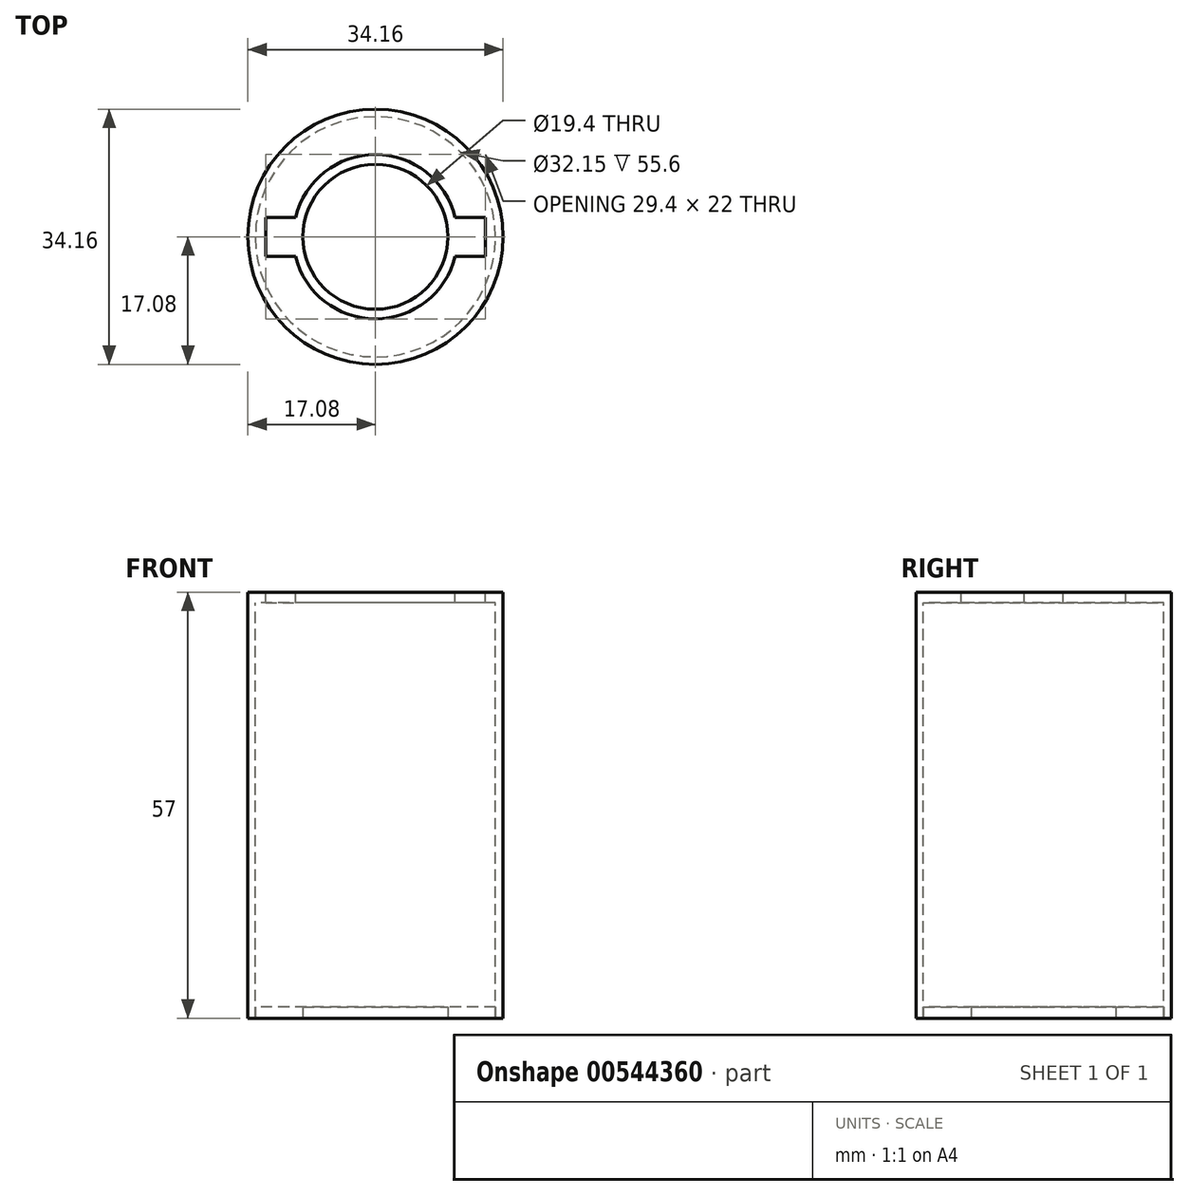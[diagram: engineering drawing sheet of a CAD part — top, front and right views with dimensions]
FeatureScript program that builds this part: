
annotation { "Feature Type Name" : "Feature", "Feature Type Description" : "" }
export const myFeature = defineFeature(function(context is Context, id is Id, definition is map)
    precondition{}
    {
        {
            var Q0;
            Q0=qCreatedBy(makeId("Top.planeOp"),FACE);
            var sketch = newSketch(context, id + "F0", { "sketchPlane" : qUnion([Q0])});
            skCircle(sketch, "E0", {"center": v(0, 0) * mm, "radius": 17.07 * mm});
            skCircle(sketch, "E1", {"center": v(0, 0) * mm, "radius": 16.07 * mm});
            skSolve(sketch);
        }
        {
            var Q0;
            Q0=makeQuery(id+"F0.imprint","IMPRINT",FACE,{"disambiguationData":[TD([[makeQuery(id+"F0.imprint","IMPRINT",EDGE,{"derivedFrom":sQuery(id+"F0.wireOp",EDGE,"E0")}),1.0]])]});
            extrude(context, id + "F1", {"entities" : qUnion([Q0]), "oppositeDirection" : true, "depth" : 57 * mm, "offsetDistance" : 25 * mm});
        }
        {
            var Q0;
            Q0=makeQuery(id+"F1.opExtrude","CAP_FACE",FACE,{"disambiguationData":[OSD([sQuery(id+"F0.wireOp",EDGE,"E0"),sQuery(id+"F0.wireOp",EDGE,"E1")])],"isStart":true});
            var sketch = newSketch(context, id + "F2", { "sketchPlane" : qUnion([Q0])});
            skCircle(sketch, "E2", {"center": v(0, 0) * mm, "radius": 11 * mm});
            skLineSegment(sketch, "E3", {"start": v(-26.25, 5.5) * mm, "end": v(-26.25, 8) * mm});
            skLineSegment(sketch, "E4", {"start": v(-26.25, 8) * mm, "end": v(-22.66, 8) * mm});
            skLineSegment(sketch, "E5.MirrorCS", {"start": v(-26.25, 3) * mm, "end": v(-22.66, 3) * mm});
            skLineSegment(sketch, "E6.MirrorCS", {"start": v(-26.25, 5.5) * mm, "end": v(-26.25, 3) * mm});
            skLineSegment(sketch, "E7", {"start": v(-11, 0) * mm, "end": v(-14.7, 0) * mm, "construction": true});
            skLineSegment(sketch, "E8", {"start": v(-14.7, 0) * mm, "end": v(-14.7, 2.6) * mm});
            skLineSegment(sketch, "E9", {"start": v(-14.7, 2.6) * mm, "end": v(-10.69, 2.6) * mm});
            skLineSegment(sketch, "E10.MirrorCS", {"start": v(-14.7, -2.6) * mm, "end": v(-10.69, -2.6) * mm});
            skLineSegment(sketch, "E11.MirrorCS", {"start": v(-14.7, 0) * mm, "end": v(-14.7, -2.6) * mm});
            skLineSegment(sketch, "E12", {"start": v(0, 11) * mm, "end": v(0, -11) * mm, "construction": true});
            skLineSegment(sketch, "E13.MirrorCS", {"start": v(14.7, -2.6) * mm, "end": v(10.69, -2.6) * mm});
            skLineSegment(sketch, "E14.MirrorCS", {"start": v(14.7, 0) * mm, "end": v(14.7, -2.6) * mm});
            skLineSegment(sketch, "E15.MirrorCS", {"start": v(14.7, 2.6) * mm, "end": v(10.69, 2.6) * mm});
            skLineSegment(sketch, "E16.MirrorCS", {"start": v(14.7, 0) * mm, "end": v(14.7, 2.6) * mm});
            skSolve(sketch);
        }
        {
            var Q0;
            Q0=makeQuery(id+"F2.imprint","IMPRINT",FACE,{"disambiguationData":[TD([[makeQuery(id+"F2.imprint","IMPRINT",EDGE,{"derivedFrom":sQuery(id+"F2.wireOp",EDGE,"E8")}),1.0]])]});
            extrude(context, id + "F3", {"entities" : qUnion([Q0]), "operationType" : NewBodyOperationType.ADD, "oppositeDirection" : true, "depth" : 1.4 * mm, "offsetDistance" : 25 * mm});
        }
        {
            var Q0;
            Q0=makeQuery(id+"F1.opExtrude","CAP_FACE",FACE,{"disambiguationData":[OSD([sQuery(id+"F0.wireOp",EDGE,"E0"),sQuery(id+"F0.wireOp",EDGE,"E1")])],"isStart":false});
            var sketch = newSketch(context, id + "F4", { "sketchPlane" : qUnion([Q0])});
            skCircle(sketch, "E17", {"center": v(0, 0) * mm, "radius": 9.7 * mm});
            skSolve(sketch);
        }
        {
            var Q0;
            Q0=makeQuery(id+"F4.imprint","IMPRINT",FACE,{"disambiguationData":[TD([[makeQuery(id+"F4.imprint","IMPRINT",EDGE,{"derivedFrom":sQuery(id+"F4.wireOp",EDGE,"E17")}),-1.0]])]});
            extrude(context, id + "F5", {"entities" : qUnion([Q0]), "oppositeDirection" : true, "depth" : 1.5 * mm, "offsetDistance" : 25 * mm});
        }
    });
